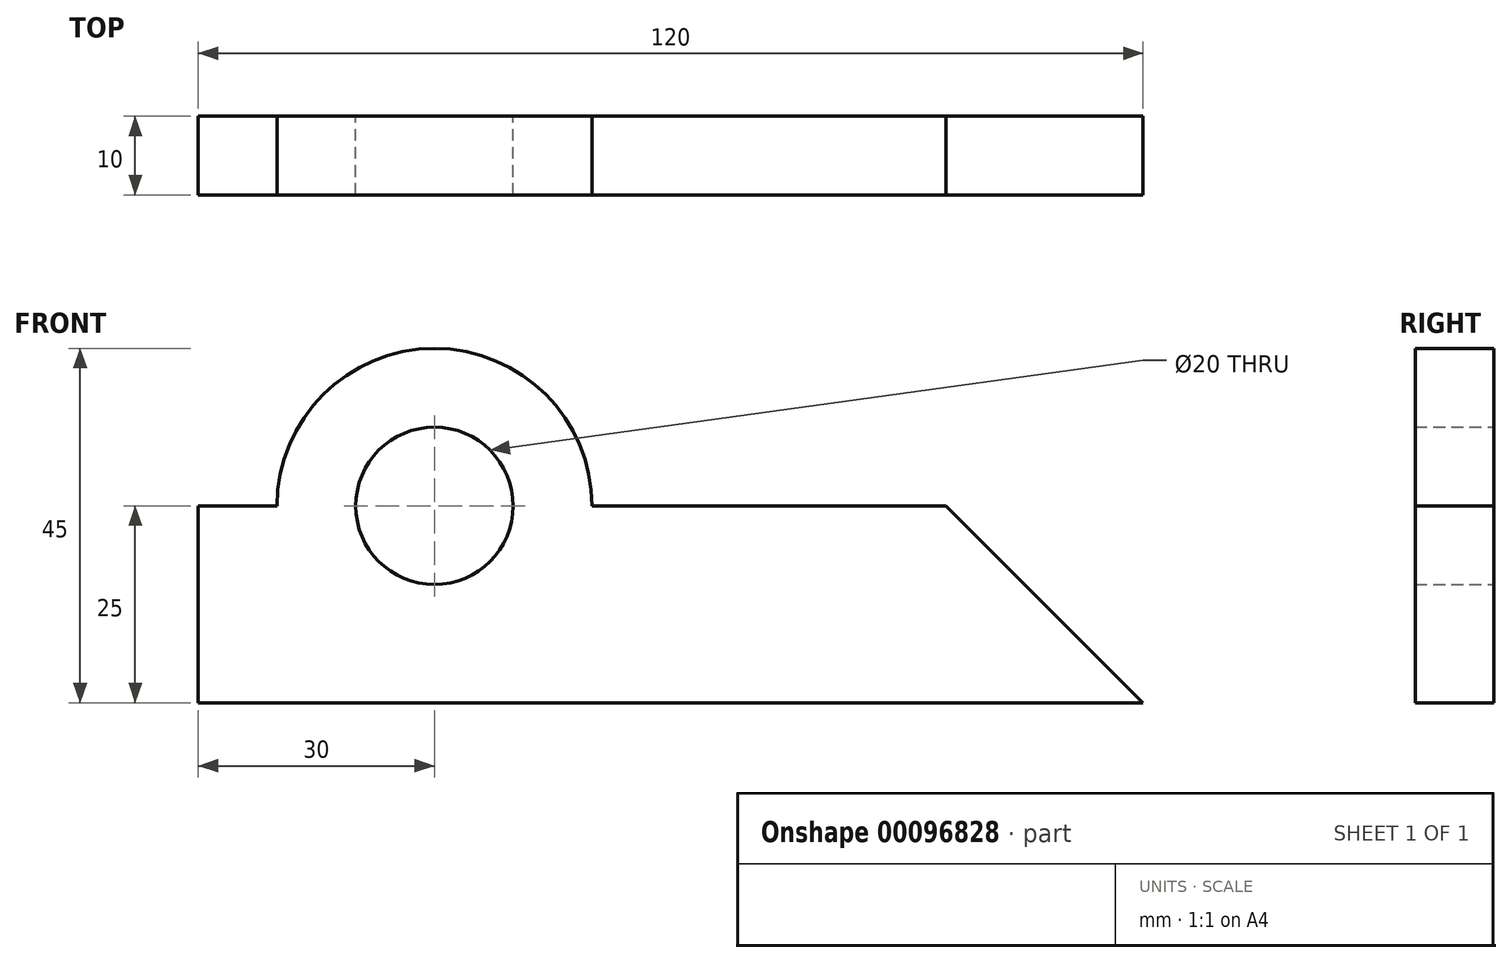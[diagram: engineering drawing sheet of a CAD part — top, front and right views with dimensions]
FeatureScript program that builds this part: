
annotation { "Feature Type Name" : "Feature", "Feature Type Description" : "" }
export const myFeature = defineFeature(function(context is Context, id is Id, definition is map)
    precondition{}
    {
        {
            var Q0;
            Q0=qCreatedBy(makeId("Front.planeOp"),FACE);
            var sketch = newSketch(context, id + "F0", { "sketchPlane" : qUnion([Q0])});
            skLineSegment(sketch, "E0", {"start": v(0, 0) * mm, "end": v(120, 0) * mm});
            skLineSegment(sketch, "E1", {"start": v(0, 0) * mm, "end": v(0, 25) * mm});
            skLineSegment(sketch, "E2", {"start": v(95, 25) * mm, "end": v(120, 0) * mm});
            skCircle(sketch, "E3", {"center": v(30, 25) * mm, "radius": 10 * mm});
            skArc(sketch, "E4", {"start": v(50, 25) * mm, "mid": v(30, 45) * mm, "end": v(10, 25) * mm});
            skLineSegment(sketch, "E5", {"start": v(10, 25) * mm, "end": v(0, 25) * mm});
            skLineSegment(sketch, "E6", {"start": v(50, 25) * mm, "end": v(95, 25) * mm});
            skSolve(sketch);
        }
        {
            var Q0;
            Q0 = qSketchRegion(id + "F0", true);
            extrude(context, id + "F1", {"entities" : qUnion([Q0]), "depth" : 10 * mm});
        }
    });
